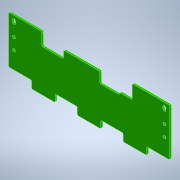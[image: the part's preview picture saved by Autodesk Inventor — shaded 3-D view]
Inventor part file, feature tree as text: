
AUTODESK INVENTOR PART (.ipt)
format: ipt  version: 2021 (Build 250183000, 183)  size: 375,296 bytes
history: native  units: mm
features: reference x36, extrude x10, other x10, sketch x9, fillet x3, projected_geometry x3
ambient origin geometry x8: Origin, YZ Plane, XZ Plane, XY Plane, X Axis, Y Axis, Z Axis, Center Point
bodies: Solid1 (feature_tree)
feature tree (71):
  extrude  "Extrusion1"  Depth=1.6mm
  extrude  "Extrusion2"  Depth=46.0mm
  extrude  "Extrusion3"  Depth=10.0mm
  extrude  "Extrusion5"  Depth=7.0mm
  extrude  "Extrusion6"  Depth=7.0mm
  extrude  "Extrusion7"  Depth=75.0mm
  extrude  "Extrusion8"  Depth=2.75mm
  fillet  "Fillet1"  Radius=2.75mm
  extrude  "Extrusion10"  Depth=5.0mm
  fillet  "Fillet2"  Radius=12.5mm
  extrude  "Extrusion11"  TaperAngle=0.0deg  [1 undecoded]
  fillet  "Fillet3"  Radius=31.0mm
  extrude  "Extrusion12"  Depth=5.0mm
  other  "FP_PCB_OUTLINE"
  sketch  "Sketch1"  dims[d0=1.6mm d1=0.0mm d2=142.0mm]
  sketch  "Sketch2"  dims[d3=46.0mm d4=43.0mm]
  projected_geometry  "Projected Loop1"
  projected_geometry  "Projected Loop2"
  sketch  "Sketch5"  dims[d5=18.0mm d6=10.0mm]
  sketch  "Sketch6"  dims[d7=0.0mm d8=0.0mm d10=7.0mm]
  sketch  "Sketch7"  dims[d11=7.0mm d15=7.0mm]
  sketch  "Sketch8"  dims[d20=0.0mm d21=0.0mm d32=75.0mm]
  projected_geometry  "Projected Loop3"
  reference  "Reference84"
  reference  "Reference85"
  reference  "Reference86"
  reference  "Reference87"
  reference  "Reference88"
  reference  "Reference89"
  reference  "Reference90"
  reference  "Reference91"
  reference  "Reference92"
  reference  "Reference93"
  reference  "Reference94"
  reference  "Reference95"
  reference  "Reference96"
  reference  "Reference97"
  reference  "Reference98"
  reference  "Reference99"
  reference  "Reference100"
  reference  "Reference101"
  reference  "Reference102"
  reference  "Reference103"
  reference  "Reference104"
  reference  "Reference105"
  reference  "Reference106"
  reference  "Reference107"
  reference  "Reference108"
  reference  "Reference109"
  reference  "Reference110"
  reference  "Reference111"
  reference  "Reference112"
  reference  "Reference113"
  reference  "Reference114"
  reference  "Reference115"
  reference  "Reference116"
  reference  "Reference117"
  reference  "Reference118"
  reference  "Reference119"
  sketch  "Sketch12"  dims[d33=0.0mm d34=0.0mm d35=2.75mm d36=2.75mm]
  sketch  "Sketch13"  dims[d37=5.0mm d38=5.0mm d39=12.5mm]
  sketch  "Sketch14"  dims[d40=10.5mm d41=0.0mm d42=0.0mm d43=31.0mm d44=5.0mm d45=5.0mm d46=10.0mm d47=0.0mm d48=2.75mm d49=2.75mm d50=5.0mm d51=5.0mm d52=5.0mm d53=5.0mm d54=0.0mm d55=0.0mm d60=1.0mm d62=22.0mm d63=22.0mm d64=12.0mm d65=20.0mm d66=0.0mm d67=0.0mm d68=1.0mm d71=0.0mm d72=0.0mm d73=1.0mm d74=13.0mm d75=12.0mm d76=0.0mm d79=0.0mm d80=0.0mm d81=2.0mm d82=53.584mm d83=53.584mm d84=22.0mm d85=11.0mm]
  other  "<userpath>\Google Drive\Unicorn 2020\CAD\Assembly.iam"
  other  "Assembly.iam"
  other  "USB_MAIN_EXTENSION_PCB_ASS:1"
  other  "TW-10-11-T-D-250-080:1"
  other  "TB2TW-10-11-T-D-250-080:1"
  other  "GSB3164X1CEU:1"
  other  "GSB3164X1CEU:3"
  other  "GSB3164X1CEU:2"
  other  "GSB3164X1CEU:4"
note: 1 required parameter value undecoded (feature->parameter linkage not recoverable at this tier; creation-order binding heuristic only, values carry confidence <= 0.55)
